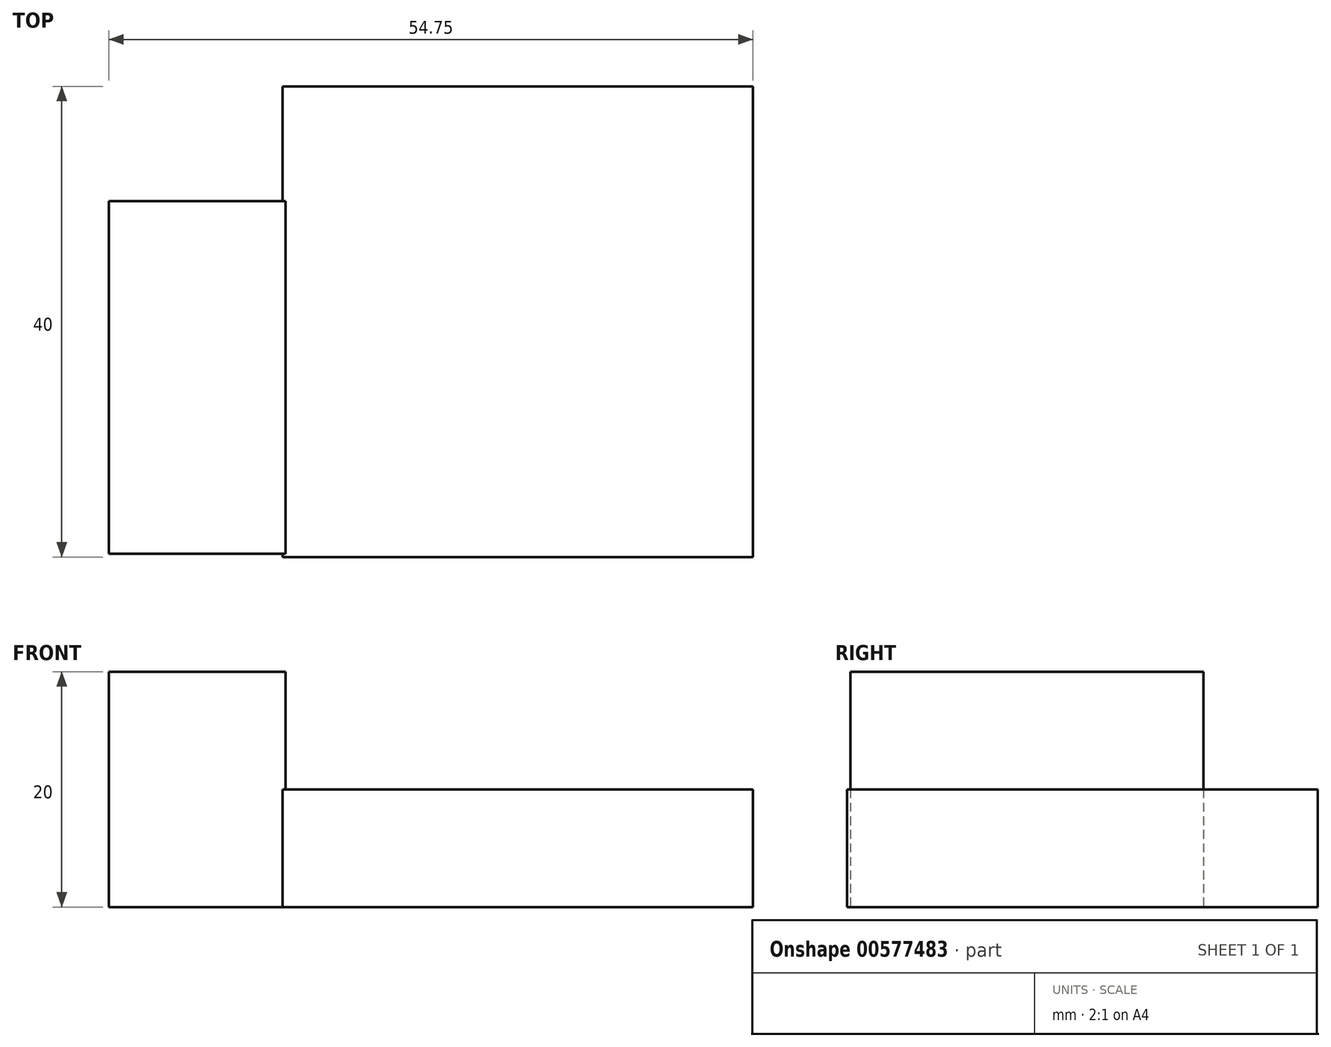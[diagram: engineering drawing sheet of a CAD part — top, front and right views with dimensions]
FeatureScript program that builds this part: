
annotation { "Feature Type Name" : "Feature", "Feature Type Description" : "" }
export const myFeature = defineFeature(function(context is Context, id is Id, definition is map)
    precondition{}
    {
        {
            var Q0;
            Q0=qCreatedBy(makeId("Top.planeOp"),FACE);
            var sketch = newSketch(context, id + "F0", { "sketchPlane" : qUnion([Q0])});
            skLineSegment(sketch, "E0.bottom", {"start": v(-17.7, 15.63) * mm, "end": v(-57.7, 15.63) * mm});
            skLineSegment(sketch, "E0.top", {"start": v(-17.7, 55.63) * mm, "end": v(-57.7, 55.63) * mm});
            skLineSegment(sketch, "E0.left", {"start": v(-17.7, 15.63) * mm, "end": v(-17.7, 55.63) * mm});
            skLineSegment(sketch, "E0.right", {"start": v(-57.7, 15.63) * mm, "end": v(-57.7, 55.63) * mm});
            skPoint(sketch, "E0.middle", {"position": v(-37.7, 35.63) * mm});
            skSolve(sketch);
        }
        {
            var Q0;
            Q0=qSketchRegion(id+"F0",true);
            var Q1;
            Q1=qConstructionFilter(qBodyType(qCreatedBy(id+"F0",EDGE),BodyType.WIRE),ConstructionObject.NO);
            extrude(context, id + "F1", {"entities" : qUnion([Q0]), "surfaceEntities" : qUnion([Q1]), "depth" : 10 * mm});
        }
        {
            var Q0;
            Q0=qCreatedBy(makeId("Top.planeOp"),FACE);
            var sketch = newSketch(context, id + "F2", { "sketchPlane" : qUnion([Q0])});
            skLineSegment(sketch, "E1.bottom", {"start": v(-72.44, 45.9) * mm, "end": v(-57.44, 45.9) * mm});
            skLineSegment(sketch, "E1.top", {"start": v(-72.44, 15.9) * mm, "end": v(-57.44, 15.9) * mm});
            skLineSegment(sketch, "E1.left", {"start": v(-72.44, 45.9) * mm, "end": v(-72.44, 15.9) * mm});
            skLineSegment(sketch, "E1.right", {"start": v(-57.44, 45.9) * mm, "end": v(-57.44, 15.9) * mm});
            skPoint(sketch, "E1.middle", {"position": v(-64.94, 30.9) * mm});
            skLineSegment(sketch, "E2.bottom", {"start": v(-211.87, -5.48) * mm, "end": v(-178.14, -5.48) * mm});
            skLineSegment(sketch, "E2.top", {"start": v(-211.87, 43.26) * mm, "end": v(-178.14, 43.26) * mm});
            skLineSegment(sketch, "E2.left", {"start": v(-211.87, -5.48) * mm, "end": v(-211.87, 43.26) * mm});
            skSolve(sketch);
        }
        {
            var Q0;
            Q0=qSketchRegion(id+"F2",true);
            extrude(context, id + "F3", {"entities" : qUnion([Q0]), "operationType" : NewBodyOperationType.ADD, "depth" : 20 * mm});
        }
    });
